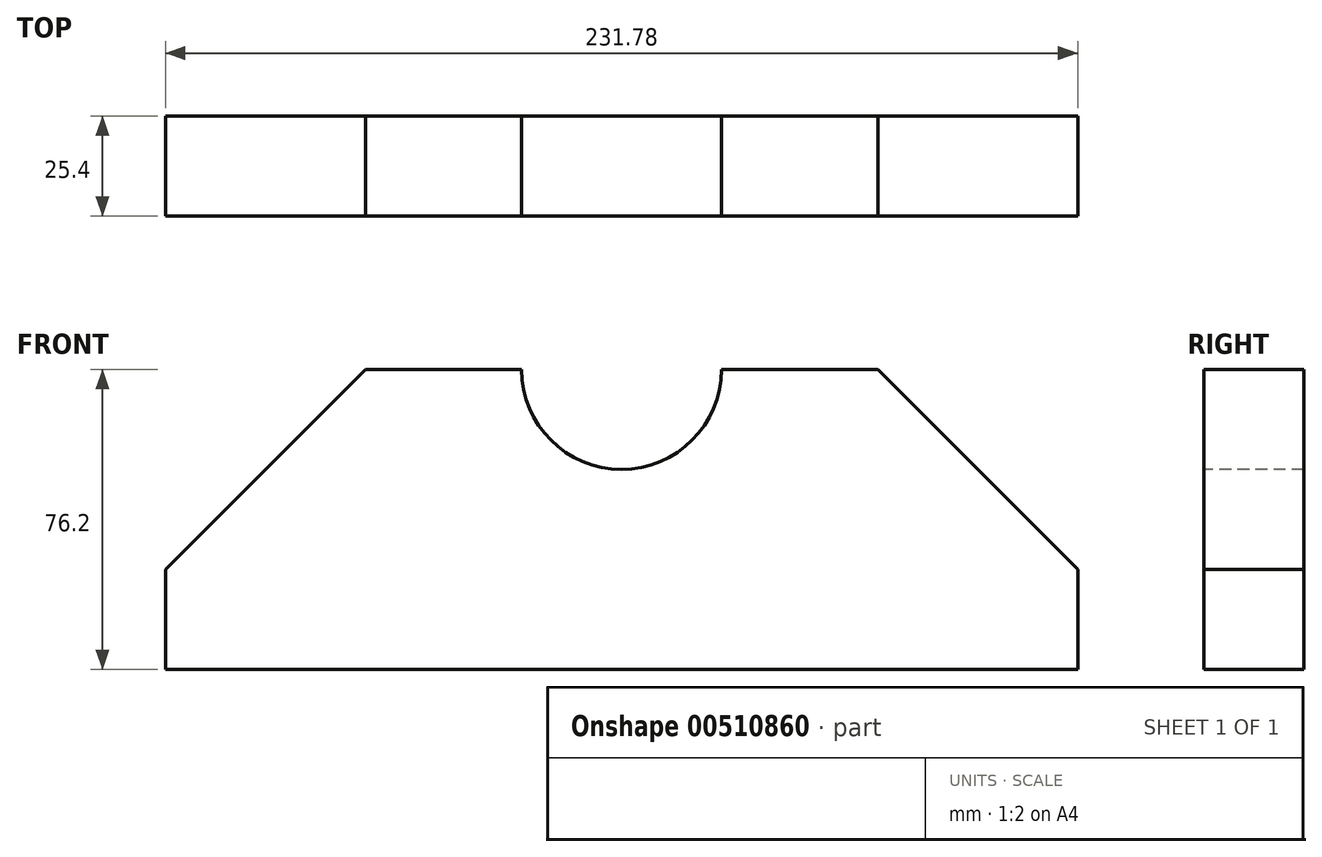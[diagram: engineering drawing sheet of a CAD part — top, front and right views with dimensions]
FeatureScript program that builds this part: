
annotation { "Feature Type Name" : "Feature", "Feature Type Description" : "" }
export const myFeature = defineFeature(function(context is Context, id is Id, definition is map)
    precondition{}
    {
        {
            var Q0;
            Q0=qCreatedBy(makeId("Top.planeOp"),FACE);
            var sketch = newSketch(context, id + "F0", { "sketchPlane" : qUnion([Q0])});
            skLineSegment(sketch, "E0.bottom", {"start": v(-215.5, 34.92) * mm, "end": v(16.27, 34.92) * mm});
            skLineSegment(sketch, "E0.top", {"start": v(-215.5, 9.52) * mm, "end": v(16.27, 9.52) * mm});
            skLineSegment(sketch, "E0.left", {"start": v(-215.5, 34.92) * mm, "end": v(-215.5, 9.52) * mm});
            skLineSegment(sketch, "E0.right", {"start": v(16.27, 34.92) * mm, "end": v(16.27, 9.52) * mm});
            skSolve(sketch);
        }
        {
            var Q0;
            Q0=makeQuery(id+"F0.imprint","IMPRINT",FACE,{"disambiguationData":[TD([[makeQuery(id+"F0.imprint","IMPRINT",EDGE,{"derivedFrom":sQuery(id+"F0.wireOp",EDGE,"E0.bottom")}),-1.0]])]});
            extrude(context, id + "F1", {"entities" : qUnion([Q0]), "depth" : 76.2 * mm, "offsetDistance" : 25.4 * mm});
        }
        {
            var Q0;
            Q0=makeQuery(id+"F1.opExtrude","CAP_EDGE",EDGE,{"disambiguationData":[OSD([sQuery(id+"F0.wireOp",EDGE,"E0.left")])],"isStart":false});
            var Q1;
            Q1=makeQuery(id+"F1.opExtrude","CAP_EDGE",EDGE,{"disambiguationData":[OSD([sQuery(id+"F0.wireOp",EDGE,"E0.right")])],"isStart":false});
            chamfer(context, id + "F2", {"entities" : qUnion([Q0, Q1]), "width" : 50.8 * mm, "tangentPropagation" : true});
        }
        {
            var Q0;
            Q0=makeQuery(id+"F1.opExtrude","SWEPT_FACE",FACE,{"disambiguationData":[OSD([sQuery(id+"F0.wireOp",EDGE,"E0.top")])]});
            var sketch = newSketch(context, id + "F3", { "sketchPlane" : qUnion([Q0])});
            skCircle(sketch, "E1", {"center": v(-99.62, 76.2) * mm, "radius": 25.4 * mm});
            skSolve(sketch);
        }
        {
            var Q0;
            {var subQ0=sQuery(id+"F3.wireOp",EDGE,"E1");var subQ1=makeQuery(id+"F1.opExtrude","CAP_EDGE",EDGE,{"disambiguationData":[OSD([sQuery(id+"F0.wireOp",EDGE,"E0.top")])],"isStart":false});var subQ2=makeQuery(id+"F3.imprint","INTERSECT",VERTEX,{"disambiguationData":[OD(0.0)],"derivedFrom":[subQ1,subQ0]});Q0=makeQuery(id+"F3.imprint","IMPRINT",FACE,{"disambiguationData":[TD([[makeQuery(id+"F3.imprint","IMPRINT",EDGE,{"disambiguationData":[TD([[subQ2,1.0]])],"derivedFrom":subQ0}),1.0]])]});}
            var Q1;
            {var subQ0=sQuery(id+"F3.wireOp",EDGE,"E1");var subQ1=makeQuery(id+"F1.opExtrude","CAP_EDGE",EDGE,{"disambiguationData":[OSD([sQuery(id+"F0.wireOp",EDGE,"E0.top")])],"isStart":false});var subQ2=makeQuery(id+"F3.imprint","INTERSECT",VERTEX,{"disambiguationData":[OD(0.0)],"derivedFrom":[subQ1,subQ0]});Q1=makeQuery(id+"F3.imprint","IMPRINT",FACE,{"disambiguationData":[TD([[makeQuery(id+"F3.imprint","IMPRINT",EDGE,{"disambiguationData":[TD([[subQ2,-1.0]])],"derivedFrom":subQ0}),1.0]])]});}
            extrude(context, id + "F4", {"entities" : qUnion([Q0, Q1]), "operationType" : NewBodyOperationType.REMOVE, "oppositeDirection" : true, "depth" : 25.4 * mm, "offsetDistance" : 25.4 * mm});
        }
    });
